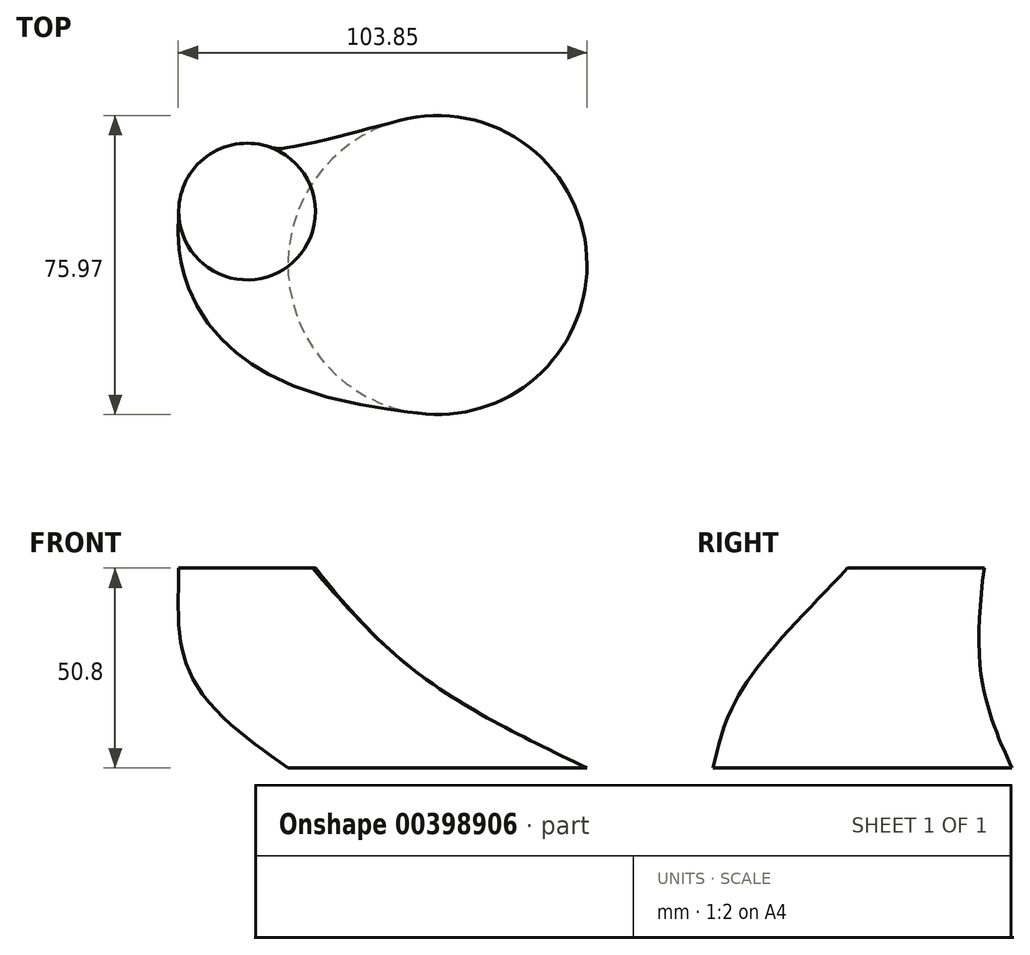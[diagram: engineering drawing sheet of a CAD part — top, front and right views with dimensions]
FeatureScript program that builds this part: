
annotation { "Feature Type Name" : "Feature", "Feature Type Description" : "" }
export const myFeature = defineFeature(function(context is Context, id is Id, definition is map)
    precondition{}
    {
        {
            var Q0;
            Q0=qCreatedBy(makeId("Top.planeOp"),FACE);
            cPlane(context, id + "F0", {"entities" : qUnion([Q0]), "cplaneType" : CPlaneType.OFFSET, "offset" : 25.4 * mm, "width" : 152.4 * mm, "height" : 152.4 * mm});
        }
        {
            var Q0;
            Q0=qCreatedBy(id+"F0.planeOp",FACE);
            cPlane(context, id + "F1", {"entities" : qUnion([Q0]), "cplaneType" : CPlaneType.OFFSET, "offset" : 25.4 * mm, "width" : 152.4 * mm, "height" : 152.4 * mm});
        }
        {
            var Q0;
            Q0=qCreatedBy(makeId("Top.planeOp"),FACE);
            var sketch = newSketch(context, id + "F2", { "sketchPlane" : qUnion([Q0])});
            skCircle(sketch, "E0", {"center": v(-11.29, -7.93) * mm, "radius": 37.98 * mm});
            skSolve(sketch);
        }
        {
            var Q0;
            Q0=qCreatedBy(id+"F0.planeOp",FACE);
            var sketch = newSketch(context, id + "F3", { "sketchPlane" : qUnion([Q0])});
            skCircle(sketch, "E1", {"center": v(-46.38, -6.37) * mm, "radius": 28.4 * mm});
            skSolve(sketch);
        }
        {
            var Q0;
            Q0=qCreatedBy(id+"F1.planeOp",FACE);
            var sketch = newSketch(context, id + "F4", { "sketchPlane" : qUnion([Q0])});
            skCircle(sketch, "E2", {"center": v(-59.66, 5.66) * mm, "radius": 17.36 * mm});
            skSolve(sketch);
        }
        {
            var Q0;
            Q0 = qSketchRegion(id + "F2", true);
            var Q1;
            Q1 = qSketchRegion(id + "F3", true);
            var Q2;
            Q2 = qSketchRegion(id + "F4", true);
            loft(context, id + "F5", {"sheetProfilesArray" : [{ "sheetProfileEntities" : qUnion([Q0]) }, { "sheetProfileEntities" : qUnion([Q1]) }, { "sheetProfileEntities" : qUnion([Q2]) }]});
        }
    });
